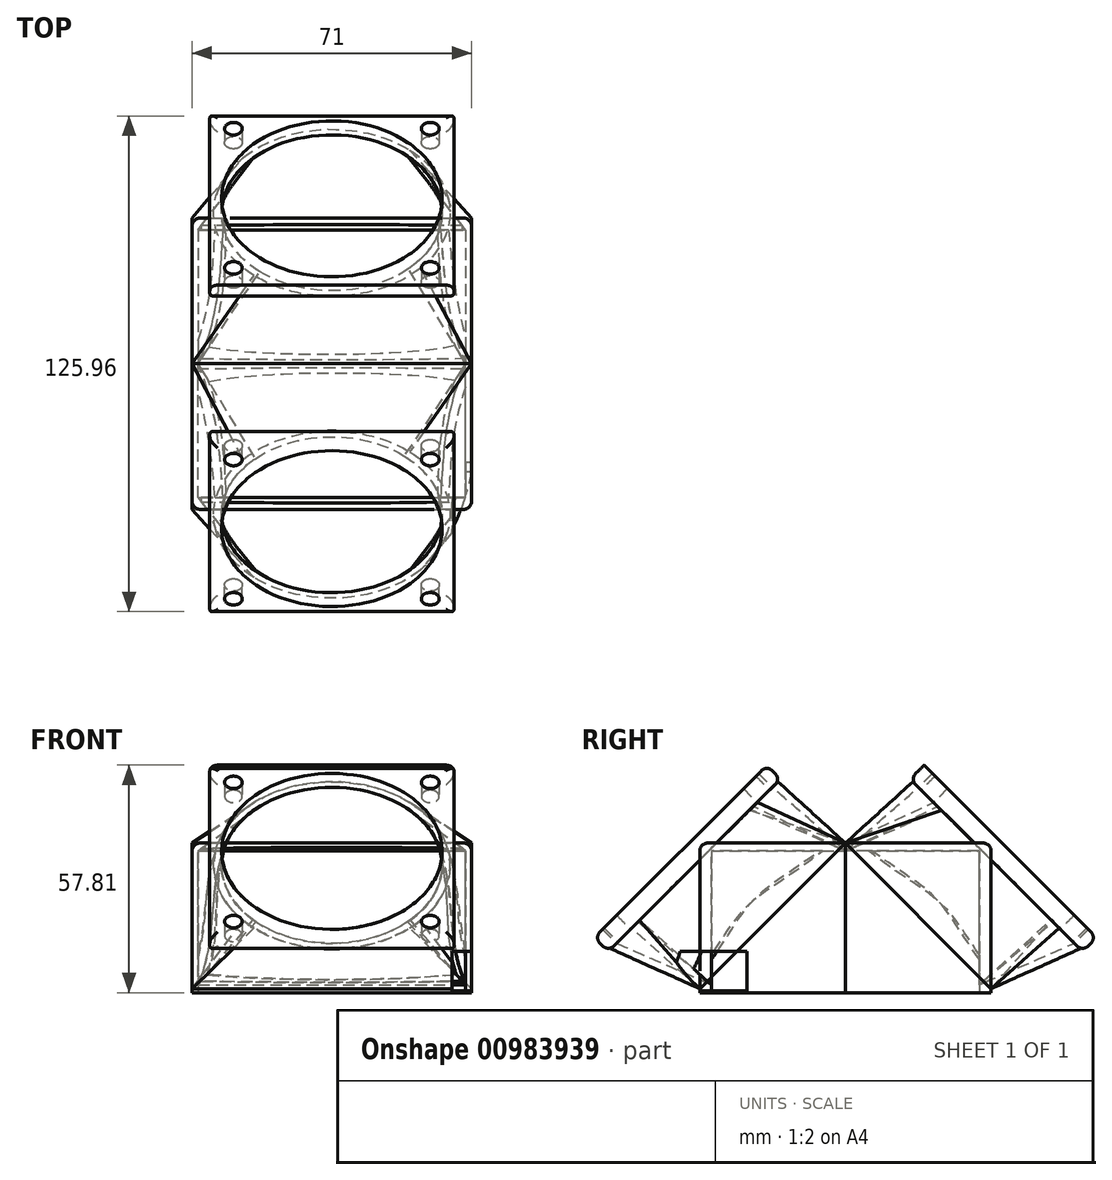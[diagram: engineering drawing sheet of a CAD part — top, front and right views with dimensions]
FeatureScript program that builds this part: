
annotation { "Feature Type Name" : "Feature", "Feature Type Description" : "" }
export const myFeature = defineFeature(function(context is Context, id is Id, definition is map)
    precondition{}
    {
        {
            var Q0;
            Q0=qCreatedBy(makeId("Front.planeOp"),FACE);
            var sketch = newSketch(context, id + "F0", { "sketchPlane" : qUnion([Q0])});
            skLineSegment(sketch, "E0.bottom", {"start": v(-34, 18) * mm, "end": v(34, 18) * mm});
            skLineSegment(sketch, "E0.top", {"start": v(-34, -18) * mm, "end": v(34, -18) * mm});
            skLineSegment(sketch, "E0.left", {"start": v(-34, 18) * mm, "end": v(-34, -18) * mm});
            skLineSegment(sketch, "E0.right", {"start": v(34, 18) * mm, "end": v(34, -18) * mm});
            skPoint(sketch, "E0.middle", {"position": v(0, 0) * mm});
            skSolve(sketch);
        }
        {
            var Q0;
            Q0=makeQuery(id+"F0.imprint","IMPRINT",FACE,{"disambiguationData":[TD([[makeQuery(id+"F0.imprint","IMPRINT",EDGE,{"derivedFrom":sQuery(id+"F0.wireOp",EDGE,"E0.bottom")}),-1.0]])]});
            extrude(context, id + "F1", {"entities" : qUnion([Q0]), "depth" : 34 * mm, "offsetDistance" : 25 * mm});
        }
        {
            var Q0;
            Q0=makeQuery(id+"F1.opExtrude","CAP_FACE",FACE,{"disambiguationData":[OSD([sQuery(id+"F0.wireOp",EDGE,"E0.bottom"),sQuery(id+"F0.wireOp",EDGE,"E0.top"),sQuery(id+"F0.wireOp",EDGE,"E0.left"),sQuery(id+"F0.wireOp",EDGE,"E0.right")])],"isStart":false});
            var sketch = newSketch(context, id + "F2", { "sketchPlane" : qUnion([Q0])});
            skLineSegment(sketch, "E1", {"start": v(-34, 0) * mm, "end": v(34, 0) * mm, "construction": true});
            skSolve(sketch);
        }
        {
            var Q0;
            Q0=sQuery(id+"F0.wireOp",EDGE,"E0.top");
            cPlane(context, id + "F3", {"entities" : qUnion([Q0]), "cplaneType" : CPlaneType.LINE_ANGLE, "offset" : 25 * mm, "angle" : 45 * degree, "oppositeDirection" : true, "width" : 150 * mm, "height" : 150 * mm});
        }
        {
            var Q0;
            Q0=sQuery(id+"F0.wireOp",EDGE,"E0.bottom");
            cPlane(context, id + "F4", {"entities" : qUnion([Q0]), "cplaneType" : CPlaneType.LINE_ANGLE, "offset" : 25 * mm, "angle" : 45 * degree, "oppositeDirection" : true, "width" : 150 * mm, "height" : 150 * mm});
        }
        {
            var Q0;
            Q0=qCreatedBy(id+"F4.planeOp",FACE);
            var sketch = newSketch(context, id + "F5", { "sketchPlane" : qUnion([Q0])});
            skLineSegment(sketch, "E2.bottom", {"start": v(-34, 12.73) * mm, "end": v(34, 12.73) * mm});
            skLineSegment(sketch, "E2.top", {"start": v(-34, -35.36) * mm, "end": v(34, -35.36) * mm});
            skLineSegment(sketch, "E2.left", {"start": v(-34, 12.73) * mm, "end": v(-34, -35.36) * mm});
            skLineSegment(sketch, "E2.right", {"start": v(34, 12.73) * mm, "end": v(34, -35.36) * mm});
            skSolve(sketch);
        }
        {
            var Q0;
            Q0=qCreatedBy(id+"F3.planeOp",FACE);
            cPlane(context, id + "F6", {"entities" : qUnion([Q0]), "cplaneType" : CPlaneType.OFFSET, "offset" : 50 * mm, "oppositeDirection" : true, "width" : 150 * mm, "height" : 150 * mm});
        }
        {
            var Q0;
            Q0=qCreatedBy(id+"F6.planeOp",FACE);
            var sketch = newSketch(context, id + "F7", { "sketchPlane" : qUnion([Q0])});
            skArc(sketch, "E3", {"start": v(19.5, 3.13) * mm, "mid": v(0.77, 11.02) * mm, "end": v(-18.36, 4.17) * mm});
            skArc(sketch, "E4", {"start": v(-18.36, 4.17) * mm, "mid": v(-27.98, -15.87) * mm, "end": v(-19.97, -36.6) * mm});
            skArc(sketch, "E5", {"start": v(-19.97, -36.6) * mm, "mid": v(-0.48, -44.97) * mm, "end": v(19.28, -37.27) * mm});
            skArc(sketch, "E6", {"start": v(19.28, -37.27) * mm, "mid": v(28, -17.12) * mm, "end": v(19.5, 3.13) * mm});
            skSolve(sketch);
        }
        {
            var Q0;
            Q0=qSketchRegion(id+"F5",true);
            var Q1;
            Q1=makeQuery(id+"F7.imprint","IMPRINT",FACE,{"disambiguationData":[TD([[makeQuery(id+"F7.imprint","IMPRINT",EDGE,{"derivedFrom":sQuery(id+"F7.wireOp",EDGE,"E3")}),1.0]])]});
            loft(context, id + "F8", {"sheetProfilesArray" : [{ "sheetProfileEntities" : qUnion([Q0]) }, { "sheetProfileEntities" : qUnion([Q1]) }]});
        }
        {
            var Q0;
            Q0=makeQuery(id+"F0.imprint","IMPRINT",FACE,{"disambiguationData":[TD([[makeQuery(id+"F0.imprint","IMPRINT",EDGE,{"derivedFrom":sQuery(id+"F0.wireOp",EDGE,"E0.bottom")}),-1.0]])]});
            var sketch = newSketch(context, id + "F9", { "sketchPlane" : qUnion([Q0])});
            skLineSegment(sketch, "E7", {"start": v(0, 18) * mm, "end": v(0, -18) * mm, "construction": true});
            skSolve(sketch);
        }
        {
            var Q0;
            Q0=makeQuery(id+"F9.imprint","IMPRINT",FACE,{"disambiguationData":[TD([[makeQuery(id+"F9.imprint","IMPRINT",EDGE,{"derivedFrom":makeQuery(id+"F0.imprint","IMPRINT",EDGE,{"derivedFrom":sQuery(id+"F0.wireOp",EDGE,"E0.bottom")})}),-1.0]])]});
            var sketch = newSketch(context, id + "F10", { "sketchPlane" : qUnion([Q0])});
            skLineSegment(sketch, "E8.bottom", {"start": v(35.5, 20) * mm, "end": v(-35.5, 20) * mm});
            skLineSegment(sketch, "E8.top", {"start": v(35.5, -18) * mm, "end": v(-35.5, -18) * mm});
            skLineSegment(sketch, "E8.left", {"start": v(35.5, 20) * mm, "end": v(35.5, -18) * mm});
            skLineSegment(sketch, "E8.right", {"start": v(-35.5, 20) * mm, "end": v(-35.5, -18) * mm});
            skPoint(sketch, "E8.middle", {"position": v(0, 0) * mm});
            skSolve(sketch);
        }
        {
            var Q0;
            Q0=qSketchRegion(id+"F10",true);
            extrude(context, id + "F11", {"entities" : qUnion([Q0]), "depth" : 37 * mm, "offsetDistance" : 25 * mm});
        }
        {
            var Q0;
            Q0=sQuery(id+"F10.wireOp",EDGE,"E8.bottom");
            cPlane(context, id + "F12", {"entities" : qUnion([Q0]), "cplaneType" : CPlaneType.LINE_ANGLE, "offset" : 25 * mm, "angle" : 45 * degree, "width" : 150 * mm, "height" : 150 * mm});
        }
        {
            var Q0;
            Q0=qCreatedBy(id+"F12.planeOp",FACE);
            var sketch = newSketch(context, id + "F13", { "sketchPlane" : qUnion([Q0])});
            skLineSegment(sketch, "E9.bottom", {"start": v(-35.5, 14.14) * mm, "end": v(35.5, 14.14) * mm});
            skLineSegment(sketch, "E9.top", {"start": v(-35.5, -38.18) * mm, "end": v(35.5, -38.18) * mm});
            skLineSegment(sketch, "E9.left", {"start": v(-35.5, 14.14) * mm, "end": v(-35.5, -38.18) * mm});
            skLineSegment(sketch, "E9.right", {"start": v(35.5, 14.14) * mm, "end": v(35.5, -38.18) * mm});
            skSolve(sketch);
        }
        {
            var Q0;
            Q0=qCreatedBy(id+"F6.planeOp",FACE);
            var sketch = newSketch(context, id + "F14", { "sketchPlane" : qUnion([Q0])});
            skCircle(sketch, "E10", {"center": v(0, -16.97) * mm, "radius": 30 * mm});
            skSolve(sketch);
        }
        {
            var Q0;
            Q0=qCreatedBy(id+"F6.planeOp",FACE);
            var sketch = newSketch(context, id + "F15", { "sketchPlane" : qUnion([Q0])});
            skLineSegment(sketch, "E11.bottom", {"start": v(-31, -47.97) * mm, "end": v(31, -47.97) * mm});
            skLineSegment(sketch, "E11.top", {"start": v(-31, 14.03) * mm, "end": v(31, 14.03) * mm});
            skLineSegment(sketch, "E11.left", {"start": v(-31, -47.97) * mm, "end": v(-31, 14.03) * mm});
            skLineSegment(sketch, "E11.right", {"start": v(31, -47.97) * mm, "end": v(31, 14.03) * mm});
            skPoint(sketch, "E11.middle", {"position": v(0, -16.97) * mm});
            skSolve(sketch);
        }
        {
            var Q0;
            Q0=qCreatedBy(id+"F6.planeOp",FACE);
            var sketch = newSketch(context, id + "F16", { "sketchPlane" : qUnion([Q0])});
            skLineSegment(sketch, "E12.bottom", {"start": v(-25, -42.18) * mm, "end": v(25, -42.18) * mm, "construction": true});
            skLineSegment(sketch, "E12.top", {"start": v(-25, 7.82) * mm, "end": v(25, 7.82) * mm, "construction": true});
            skLineSegment(sketch, "E12.left", {"start": v(-25, -42.18) * mm, "end": v(-25, 7.82) * mm, "construction": true});
            skLineSegment(sketch, "E12.right", {"start": v(25, -42.18) * mm, "end": v(25, 7.82) * mm, "construction": true});
            skPoint(sketch, "E12.middle", {"position": v(0, -17.18) * mm});
            skSolve(sketch);
        }
        {
            var Q0;
            Q0=qCreatedBy(id+"F6.planeOp",FACE);
            var sketch = newSketch(context, id + "F17", { "sketchPlane" : qUnion([Q0])});
            skCircle(sketch, "E13", {"center": v(25, -42.18) * mm, "radius": 2.25 * mm});
            skCircle(sketch, "E14", {"center": v(-25, -42.18) * mm, "radius": 2.25 * mm});
            skCircle(sketch, "E15", {"center": v(-25, 7.82) * mm, "radius": 2.25 * mm});
            skCircle(sketch, "E16", {"center": v(25, 7.82) * mm, "radius": 2.25 * mm});
            skSolve(sketch);
        }
        {
            var Q0;
            Q0=makeQuery(id+"F8.opLoft","CAP_FACE",FACE,{"disambiguationData":[OSD([makeQuery(id+"F7.imprint","IMPRINT",FACE,{"disambiguationData":[TD([[makeQuery(id+"F7.imprint","IMPRINT",EDGE,{"derivedFrom":sQuery(id+"F7.wireOp",EDGE,"E3")}),1.0]])]})])],"isStart":true});
            var Q1;
            Q1=makeQuery(id+"F17.imprint","IMPRINT",FACE,{"disambiguationData":[TD([[makeQuery(id+"F17.imprint","IMPRINT",EDGE,{"derivedFrom":sQuery(id+"F17.wireOp",EDGE,"E16")}),1.0]])]});
            var Q2;
            Q2=makeQuery(id+"F17.imprint","IMPRINT",FACE,{"disambiguationData":[TD([[makeQuery(id+"F17.imprint","IMPRINT",EDGE,{"derivedFrom":sQuery(id+"F17.wireOp",EDGE,"E15")}),1.0]])]});
            var Q3;
            Q3=makeQuery(id+"F17.imprint","IMPRINT",FACE,{"disambiguationData":[TD([[makeQuery(id+"F17.imprint","IMPRINT",EDGE,{"derivedFrom":sQuery(id+"F17.wireOp",EDGE,"E14")}),1.0]])]});
            var Q4;
            Q4=makeQuery(id+"F17.imprint","IMPRINT",FACE,{"disambiguationData":[TD([[makeQuery(id+"F17.imprint","IMPRINT",EDGE,{"derivedFrom":sQuery(id+"F17.wireOp",EDGE,"E13")}),1.0]])]});
            extrude(context, id + "F18", {"entities" : qUnion([Q0, Q1, Q2, Q3, Q4]), "depth" : 5 * mm, "offsetDistance" : 25 * mm});
        }
        {
            var Q0;
            Q0=makeQuery(id+"F13.imprint","IMPRINT",FACE,{"disambiguationData":[TD([[makeQuery(id+"F13.imprint","IMPRINT",EDGE,{"derivedFrom":sQuery(id+"F13.wireOp",EDGE,"E9.bottom")}),-1.0]])]});
            var Q1;
            Q1=qSketchRegion(id+"F14",true);
            loft(context, id + "F19", {"sheetProfilesArray" : [{ "sheetProfileEntities" : qUnion([Q0]) }, { "sheetProfileEntities" : qUnion([Q1]) }]});
        }
        {
            var Q0;
            Q0=makeQuery(id+"F15.imprint","IMPRINT",FACE,{"disambiguationData":[TD([[makeQuery(id+"F15.imprint","IMPRINT",EDGE,{"derivedFrom":sQuery(id+"F15.wireOp",EDGE,"E11.bottom")}),1.0]])]});
            extrude(context, id + "F20", {"entities" : qUnion([Q0]), "oppositeDirection" : true, "depth" : 5 * mm, "offsetDistance" : 25 * mm});
        }
        {
            var Q0;
            Q0=makeQuery(id+"F18.opExtrude","SWEPT_BODY",BODY,{"disambiguationData":[OSD([sQuery(id+"F17.wireOp",EDGE,"E16")])]});
            var Q1;
            Q1=makeQuery(id+"F18.opExtrude","SWEPT_BODY",BODY,{"disambiguationData":[OSD([sQuery(id+"F17.wireOp",EDGE,"E15")])]});
            var Q2;
            Q2=makeQuery(id+"F18.opExtrude","SWEPT_BODY",BODY,{"disambiguationData":[OSD([sQuery(id+"F17.wireOp",EDGE,"E14")])]});
            var Q3;
            Q3=makeQuery(id+"F18.opExtrude","SWEPT_BODY",BODY,{"disambiguationData":[OSD([sQuery(id+"F17.wireOp",EDGE,"E13")])]});
            var Q4;
            Q4=makeQuery(id+"F18.opExtrude","SWEPT_BODY",BODY,{"disambiguationData":[OSD([makeQuery(id+"F7.imprint","IMPRINT",FACE,{"disambiguationData":[TD([[makeQuery(id+"F7.imprint","IMPRINT",EDGE,{"derivedFrom":sQuery(id+"F7.wireOp",EDGE,"E3")}),1.0]])]})])]});
            var Q5;
            Q5=makeQuery(id+"F8.opLoft","SWEPT_BODY",BODY,{"disambiguationData":[OSD([makeQuery(id+"F5.imprint","IMPRINT",FACE,{"disambiguationData":[TD([[makeQuery(id+"F5.imprint","IMPRINT",EDGE,{"derivedFrom":sQuery(id+"F5.wireOp",EDGE,"E2.bottom")}),-1.0]])]}),makeQuery(id+"F7.imprint","IMPRINT",FACE,{"disambiguationData":[TD([[makeQuery(id+"F7.imprint","IMPRINT",EDGE,{"derivedFrom":sQuery(id+"F7.wireOp",EDGE,"E3")}),1.0]])]})])]});
            var Q6;
            Q6=makeQuery(id+"F1.opExtrude","SWEPT_BODY",BODY,{"disambiguationData":[OSD([sQuery(id+"F0.wireOp",EDGE,"E0.bottom"),sQuery(id+"F0.wireOp",EDGE,"E0.top"),sQuery(id+"F0.wireOp",EDGE,"E0.left"),sQuery(id+"F0.wireOp",EDGE,"E0.right")])]});
            var Q7;
            Q7=makeQuery(id+"F11.opExtrude","SWEPT_BODY",BODY,{"disambiguationData":[OSD([sQuery(id+"F10.wireOp",EDGE,"E8.bottom"),sQuery(id+"F10.wireOp",EDGE,"E8.top"),sQuery(id+"F10.wireOp",EDGE,"E8.left"),sQuery(id+"F10.wireOp",EDGE,"E8.right")])]});
            var Q8;
            Q8=makeQuery(id+"F19.opLoft","SWEPT_BODY",BODY,{"disambiguationData":[OSD([makeQuery(id+"F13.imprint","IMPRINT",FACE,{"disambiguationData":[TD([[makeQuery(id+"F13.imprint","IMPRINT",EDGE,{"derivedFrom":sQuery(id+"F13.wireOp",EDGE,"E9.bottom")}),-1.0]])]}),makeQuery(id+"F14.imprint","IMPRINT",FACE,{"disambiguationData":[TD([[makeQuery(id+"F14.imprint","IMPRINT",EDGE,{"derivedFrom":sQuery(id+"F14.wireOp",EDGE,"E10")}),1.0]])]})])]});
            var Q9;
            Q9=makeQuery(id+"F20.opExtrude","SWEPT_BODY",BODY,{"disambiguationData":[OSD([sQuery(id+"F15.wireOp",EDGE,"E11.bottom"),sQuery(id+"F15.wireOp",EDGE,"E11.top"),sQuery(id+"F15.wireOp",EDGE,"E11.left"),sQuery(id+"F15.wireOp",EDGE,"E11.right")])]});
            booleanBodies(context, id + "F21", {"operationType" : BooleanOperationType.SUBTRACTION, "tools" : qUnion([Q0, Q1, Q2, Q3, Q4, Q5, Q6]), "targets" : qUnion([Q7, Q8, Q9])});
        }
        {
            var Q0;
            Q0=makeQuery(id+"F11.opExtrude","SWEPT_BODY",BODY,{"disambiguationData":[OSD([sQuery(id+"F10.wireOp",EDGE,"E8.bottom"),sQuery(id+"F10.wireOp",EDGE,"E8.top"),sQuery(id+"F10.wireOp",EDGE,"E8.left"),sQuery(id+"F10.wireOp",EDGE,"E8.right")])]});
            var Q1;
            Q1=sQuery(id+"F9.wireOp",EDGE,"E7");
            transform(context, id + "F22", {"entities" : qUnion([Q0]), "transformType" : TransformType.ROTATION, "transformAxis" : qUnion([Q1]), "angle" : 180 * degree, "makeCopy" : true});
        }
        {
            var Q0;
            Q0=makeQuery(id+"F19.opLoft","SWEPT_BODY",BODY,{"disambiguationData":[OSD([makeQuery(id+"F13.imprint","IMPRINT",FACE,{"disambiguationData":[TD([[makeQuery(id+"F13.imprint","IMPRINT",EDGE,{"derivedFrom":sQuery(id+"F13.wireOp",EDGE,"E9.bottom")}),-1.0]])]}),makeQuery(id+"F14.imprint","IMPRINT",FACE,{"disambiguationData":[TD([[makeQuery(id+"F14.imprint","IMPRINT",EDGE,{"derivedFrom":sQuery(id+"F14.wireOp",EDGE,"E10")}),1.0]])]})])]});
            var Q1;
            Q1=sQuery(id+"F9.wireOp",EDGE,"E7");
            transform(context, id + "F23", {"entities" : qUnion([Q0]), "transformType" : TransformType.ROTATION, "transformAxis" : qUnion([Q1]), "angle" : 180 * degree, "makeCopy" : true});
        }
        {
            var Q0;
            Q0=makeQuery(id+"F20.opExtrude","SWEPT_BODY",BODY,{"disambiguationData":[OSD([sQuery(id+"F15.wireOp",EDGE,"E11.bottom"),sQuery(id+"F15.wireOp",EDGE,"E11.top"),sQuery(id+"F15.wireOp",EDGE,"E11.left"),sQuery(id+"F15.wireOp",EDGE,"E11.right")])]});
            var Q1;
            Q1=sQuery(id+"F9.wireOp",EDGE,"E7");
            transform(context, id + "F24", {"entities" : qUnion([Q0]), "transformType" : TransformType.ROTATION, "transformAxis" : qUnion([Q1]), "angle" : 180 * degree, "makeCopy" : true});
        }
        {
            var Q0;
            Q0=makeQuery(id+"F20.opExtrude","CAP_EDGE",EDGE,{"disambiguationData":[OSD([sQuery(id+"F15.wireOp",EDGE,"E11.left")])],"isStart":false});
            var Q1;
            Q1=makeQuery(id+"F20.opExtrude","CAP_EDGE",EDGE,{"disambiguationData":[OSD([sQuery(id+"F15.wireOp",EDGE,"E11.top")])],"isStart":false});
            var Q2;
            Q2=makeQuery(id+"F20.opExtrude","CAP_EDGE",EDGE,{"disambiguationData":[OSD([sQuery(id+"F15.wireOp",EDGE,"E11.right")])],"isStart":false});
            var Q3;
            Q3=makeQuery(id+"F20.opExtrude","CAP_EDGE",EDGE,{"disambiguationData":[OSD([sQuery(id+"F15.wireOp",EDGE,"E11.bottom")])],"isStart":false});
            var Q4;
            Q4=makeQuery(id+"F20.opExtrude","CAP_EDGE",EDGE,{"disambiguationData":[OSD([sQuery(id+"F15.wireOp",EDGE,"E11.left")])],"isStart":true});
            var Q5;
            Q5=makeQuery(id+"F20.opExtrude","CAP_EDGE",EDGE,{"disambiguationData":[OSD([sQuery(id+"F15.wireOp",EDGE,"E11.bottom")])],"isStart":true});
            var Q6;
            Q6=makeQuery(id+"F20.opExtrude","CAP_EDGE",EDGE,{"disambiguationData":[OSD([sQuery(id+"F15.wireOp",EDGE,"E11.right")])],"isStart":true});
            var Q7;
            Q7=makeQuery(id+"F20.opExtrude","CAP_EDGE",EDGE,{"disambiguationData":[OSD([sQuery(id+"F15.wireOp",EDGE,"E11.top")])],"isStart":true});
            var Q8;
            Q8=makeQuery(id+"F11.opExtrude","CAP_EDGE",EDGE,{"disambiguationData":[OSD([sQuery(id+"F10.wireOp",EDGE,"E8.right")])],"isStart":false});
            var Q9;
            {var subQ0=sQuery(id+"F10.wireOp",EDGE,"E8.bottom");var subQ1=sQuery(id+"F10.wireOp",EDGE,"E8.right");Q9=makeQuery(id+"F21.opBoolean","SPLIT",EDGE,{"disambiguationData":[TD([makeQuery(id+"F11.opExtrude","SWEPT_FACE",FACE,{"disambiguationData":[OSD([subQ1])]})])],"derivedFrom":makeQuery(id+"F11.opExtrude","CAP_EDGE",EDGE,{"disambiguationData":[OSD([subQ0])],"isStart":false})});}
            var Q10;
            Q10=makeQuery(id+"F11.opExtrude","SWEPT_EDGE",EDGE,{"disambiguationData":[OSD([sQuery(id+"F10.wireOp",EDGE,"E8.bottom"),sQuery(id+"F10.wireOp",EDGE,"E8.right")])]});
            var Q11;
            Q11=makeQuery(id+"F11.opExtrude","CAP_EDGE",EDGE,{"disambiguationData":[OSD([sQuery(id+"F10.wireOp",EDGE,"E8.left")])],"isStart":false});
            var Q12;
            Q12=makeQuery(id+"F11.opExtrude","SWEPT_EDGE",EDGE,{"disambiguationData":[OSD([sQuery(id+"F10.wireOp",EDGE,"E8.bottom"),sQuery(id+"F10.wireOp",EDGE,"E8.left")])]});
            var Q13;
            {var subQ0=sQuery(id+"F10.wireOp",EDGE,"E8.bottom");var subQ1=sQuery(id+"F10.wireOp",EDGE,"E8.left");Q13=makeQuery(id+"F21.opBoolean","SPLIT",EDGE,{"disambiguationData":[TD([makeQuery(id+"F11.opExtrude","SWEPT_FACE",FACE,{"disambiguationData":[OSD([subQ1])]})])],"derivedFrom":makeQuery(id+"F11.opExtrude","CAP_EDGE",EDGE,{"disambiguationData":[OSD([subQ0])],"isStart":false})});}
            var Q14;
            Q14=makeQuery(id+"F22.opPattern","COPY",EDGE,{"derivedFrom":makeQuery(id+"F11.opExtrude","SWEPT_EDGE",EDGE,{"disambiguationData":[OSD([sQuery(id+"F10.wireOp",EDGE,"E8.bottom"),sQuery(id+"F10.wireOp",EDGE,"E8.right")])]}),"instanceName":"1"});
            var Q15;
            {var subQ0=sQuery(id+"F10.wireOp",EDGE,"E8.bottom");var subQ1=sQuery(id+"F10.wireOp",EDGE,"E8.right");Q15=makeQuery(id+"F22.opPattern","COPY",EDGE,{"derivedFrom":makeQuery(id+"F21.opBoolean","SPLIT",EDGE,{"disambiguationData":[TD([makeQuery(id+"F11.opExtrude","SWEPT_FACE",FACE,{"disambiguationData":[OSD([subQ1])]})])],"derivedFrom":makeQuery(id+"F11.opExtrude","CAP_EDGE",EDGE,{"disambiguationData":[OSD([subQ0])],"isStart":false})}),"instanceName":"1"});}
            var Q16;
            Q16=makeQuery(id+"F22.opPattern","COPY",EDGE,{"derivedFrom":makeQuery(id+"F11.opExtrude","CAP_EDGE",EDGE,{"disambiguationData":[OSD([sQuery(id+"F10.wireOp",EDGE,"E8.right")])],"isStart":false}),"instanceName":"1"});
            var Q17;
            Q17=makeQuery(id+"F24.opPattern","COPY",EDGE,{"derivedFrom":makeQuery(id+"F20.opExtrude","CAP_EDGE",EDGE,{"disambiguationData":[OSD([sQuery(id+"F15.wireOp",EDGE,"E11.right")])],"isStart":false}),"instanceName":"1"});
            var Q18;
            Q18=makeQuery(id+"F24.opPattern","COPY",EDGE,{"derivedFrom":makeQuery(id+"F20.opExtrude","CAP_EDGE",EDGE,{"disambiguationData":[OSD([sQuery(id+"F15.wireOp",EDGE,"E11.right")])],"isStart":true}),"instanceName":"1"});
            var Q19;
            Q19=makeQuery(id+"F24.opPattern","COPY",EDGE,{"derivedFrom":makeQuery(id+"F20.opExtrude","CAP_EDGE",EDGE,{"disambiguationData":[OSD([sQuery(id+"F15.wireOp",EDGE,"E11.top")])],"isStart":true}),"instanceName":"1"});
            var Q20;
            Q20=makeQuery(id+"F24.opPattern","COPY",EDGE,{"derivedFrom":makeQuery(id+"F20.opExtrude","CAP_EDGE",EDGE,{"disambiguationData":[OSD([sQuery(id+"F15.wireOp",EDGE,"E11.bottom")])],"isStart":true}),"instanceName":"1"});
            var Q21;
            Q21=makeQuery(id+"F24.opPattern","COPY",EDGE,{"derivedFrom":makeQuery(id+"F20.opExtrude","CAP_EDGE",EDGE,{"disambiguationData":[OSD([sQuery(id+"F15.wireOp",EDGE,"E11.bottom")])],"isStart":false}),"instanceName":"1"});
            var Q22;
            Q22=makeQuery(id+"F24.opPattern","COPY",EDGE,{"derivedFrom":makeQuery(id+"F20.opExtrude","CAP_EDGE",EDGE,{"disambiguationData":[OSD([sQuery(id+"F15.wireOp",EDGE,"E11.left")])],"isStart":false}),"instanceName":"1"});
            var Q23;
            Q23=makeQuery(id+"F24.opPattern","COPY",EDGE,{"derivedFrom":makeQuery(id+"F20.opExtrude","CAP_EDGE",EDGE,{"disambiguationData":[OSD([sQuery(id+"F15.wireOp",EDGE,"E11.left")])],"isStart":true}),"instanceName":"1"});
            var Q24;
            Q24=makeQuery(id+"F22.opPattern","COPY",EDGE,{"derivedFrom":makeQuery(id+"F11.opExtrude","CAP_EDGE",EDGE,{"disambiguationData":[OSD([sQuery(id+"F10.wireOp",EDGE,"E8.left")])],"isStart":false}),"instanceName":"1"});
            var Q25;
            {var subQ0=sQuery(id+"F10.wireOp",EDGE,"E8.bottom");var subQ1=sQuery(id+"F10.wireOp",EDGE,"E8.left");Q25=makeQuery(id+"F22.opPattern","COPY",EDGE,{"derivedFrom":makeQuery(id+"F21.opBoolean","SPLIT",EDGE,{"disambiguationData":[TD([makeQuery(id+"F11.opExtrude","SWEPT_FACE",FACE,{"disambiguationData":[OSD([subQ1])]})])],"derivedFrom":makeQuery(id+"F11.opExtrude","CAP_EDGE",EDGE,{"disambiguationData":[OSD([subQ0])],"isStart":false})}),"instanceName":"1"});}
            var Q26;
            Q26=makeQuery(id+"F22.opPattern","COPY",EDGE,{"derivedFrom":makeQuery(id+"F11.opExtrude","SWEPT_EDGE",EDGE,{"disambiguationData":[OSD([sQuery(id+"F10.wireOp",EDGE,"E8.bottom"),sQuery(id+"F10.wireOp",EDGE,"E8.left")])]}),"instanceName":"1"});
            fillet(context, id + "F25", {"entities" : qUnion([Q0, Q1, Q2, Q3, Q4, Q5, Q6, Q7, Q8, Q9, Q10, Q11, Q12, Q13, Q14, Q15, Q16, Q17, Q18, Q19, Q20, Q21, Q22, Q23, Q24, Q25, Q26]), "radius" : 2 * mm, "tangentPropagation" : true, "allowEdgeOverflow" : false});
        }
        {
            var Q0;
            Q0=makeQuery(id+"F11.opExtrude","SWEPT_FACE",FACE,{"disambiguationData":[OSD([sQuery(id+"F10.wireOp",EDGE,"E8.left")])]});
            var sketch = newSketch(context, id + "F26", { "sketchPlane" : qUnion([Q0])});
            skLineSegment(sketch, "E17.bottom", {"start": v(-25, -17.5) * mm, "end": v(-45, -17.5) * mm});
            skLineSegment(sketch, "E17.top", {"start": v(-25, -7.5) * mm, "end": v(-45, -7.5) * mm});
            skLineSegment(sketch, "E17.left", {"start": v(-25, -17.5) * mm, "end": v(-25, -7.5) * mm});
            skLineSegment(sketch, "E17.right", {"start": v(-45, -17.5) * mm, "end": v(-45, -7.5) * mm});
            skSolve(sketch);
        }
        {
            var Q0;
            Q0=qSketchRegion(id+"F26",true);
            extrude(context, id + "F27", {"entities" : qUnion([Q0]), "oppositeDirection" : true, "depth" : 5 * mm, "offsetDistance" : 25 * mm});
        }
        {
            var Q0;
            Q0=makeQuery(id+"F27.opExtrude","SWEPT_BODY",BODY,{"disambiguationData":[OSD([sQuery(id+"F26.wireOp",EDGE,"E17.bottom"),sQuery(id+"F26.wireOp",EDGE,"E17.top"),sQuery(id+"F26.wireOp",EDGE,"E17.left"),sQuery(id+"F26.wireOp",EDGE,"E17.right")])]});
            var Q1;
            Q1=makeQuery(id+"F11.opExtrude","SWEPT_BODY",BODY,{"disambiguationData":[OSD([sQuery(id+"F10.wireOp",EDGE,"E8.bottom"),sQuery(id+"F10.wireOp",EDGE,"E8.top"),sQuery(id+"F10.wireOp",EDGE,"E8.left"),sQuery(id+"F10.wireOp",EDGE,"E8.right")])]});
            var Q2;
            Q2=makeQuery(id+"F19.opLoft","SWEPT_BODY",BODY,{"disambiguationData":[OSD([makeQuery(id+"F13.imprint","IMPRINT",FACE,{"disambiguationData":[TD([[makeQuery(id+"F13.imprint","IMPRINT",EDGE,{"derivedFrom":sQuery(id+"F13.wireOp",EDGE,"E9.bottom")}),-1.0]])]}),makeQuery(id+"F14.imprint","IMPRINT",FACE,{"disambiguationData":[TD([[makeQuery(id+"F14.imprint","IMPRINT",EDGE,{"derivedFrom":sQuery(id+"F14.wireOp",EDGE,"E10")}),1.0]])]})])]});
            booleanBodies(context, id + "F28", {"operationType" : BooleanOperationType.SUBTRACTION, "tools" : qUnion([Q0]), "targets" : qUnion([Q1, Q2])});
        }
    });
